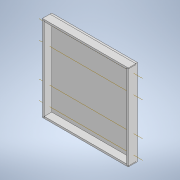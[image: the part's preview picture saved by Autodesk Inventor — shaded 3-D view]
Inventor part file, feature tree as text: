
AUTODESK INVENTOR PART (.ipt)
format: ipt  version: 2022 (Build 260153000, 153)  size: 182,272 bytes
history: native  units: mm
features: sketch x5, extrude x4, other x4, projected_geometry x3, boolean_combine x2, plane x2, mirror x2, shell x1
ambient origin geometry x8: Origin, YZ Plane, XZ Plane, XY Plane, X Axis, Y Axis, Z Axis, Center Point
bodies: Solid3 (feature_tree), Solid4 (feature_tree)
feature tree (23):
  extrude  "Extrusion3"  Depth=292.1mm
  sketch  "Sketch2"  dims[d15=88.9mm d16=88.9mm]
  shell  "Shell1"  Thickness=31.75mm
  sketch  "Sketch3"  dims[d17=6.35mm d20=25.4mm]
  other  "Work Axis3"
  other  "Work Axis4"
  other  "Work Axis5"
  other  "Work Axis6"
  sketch  "Sketch6"  dims[d24=25.4mm d25=7.271042mm d26=6.35mm d27=0.0mm d28=6.5mm d42=10.0mm d43=0.0mm d44=10.0mm d45=0.0mm]
  extrude  "Extrusion6"  Depth=88.9mm
  extrude  "Extrusion7"  Depth=25.4mm
  boolean_combine  "Combine1"
  boolean_combine  "Combine2"
  extrude  "Extrusion4"  Depth=88.9mm
  plane  "Work Plane1"
  plane  "Work Plane2"
  mirror  "Mirror1"
  mirror  "Mirror2"
  sketch  "Sketch1"  dims[d11=292.1mm d12=292.1mm d13=31.75mm d14=0.0mm]
  projected_geometry  "Projected Loop1"
  sketch  "Sketch4"  dims[d22=88.9mm d23=88.9mm]
  projected_geometry  "Projected Loop2"
  projected_geometry  "Projected Loop3"
